# Revit family: Accessory-Cutting_Board-KOHLER-Lyric-K-23379
name_source: partatom
category: Specialty Equipment
units: mm (PartAtom-declared; Revit-internal decimal feet)

## family parameters
Cut with Voids When Loaded = No
Host = Face
OmniClass Number = 23.31.25.00
OmniClass Title = Toilet and Bath Specialties
Part Type = Normal
Room Calculation Point = No
Round Connector Dimension = Use Diameter
Shared = No

## types (1)
- NA-Hinoki
    ADA Compliant = No
    Assembly Code = C1030200
    Date Modified = 12/30/2022
    Default Elevation = 0"
    Description = Cutting board
    Finish = KOHLER-Wood-NA-Hinoki
    Height = 3/4"
    Length = 17 1/2"
    Manufacturer = Kohler Co.
    Master Format 2014 = 10 28 00
    Master Format 2014 Name = Toilet, Bath, and Laundry Accessories
    Material = Wood Construction
    Model = K-23379-NA
    Product Documentation Link = https://www.us.kohler.com
    Product Name = Lyric
    Product Page URL = http://www.us.kohler.com
    Type = 1
    URL = https://www.us.kohler.com
    WaterSense Certified = No
    Width = 12"

## geometry (parser evidence)
native form markers: Sweep x6
no freeform markers — native parametric forms only
